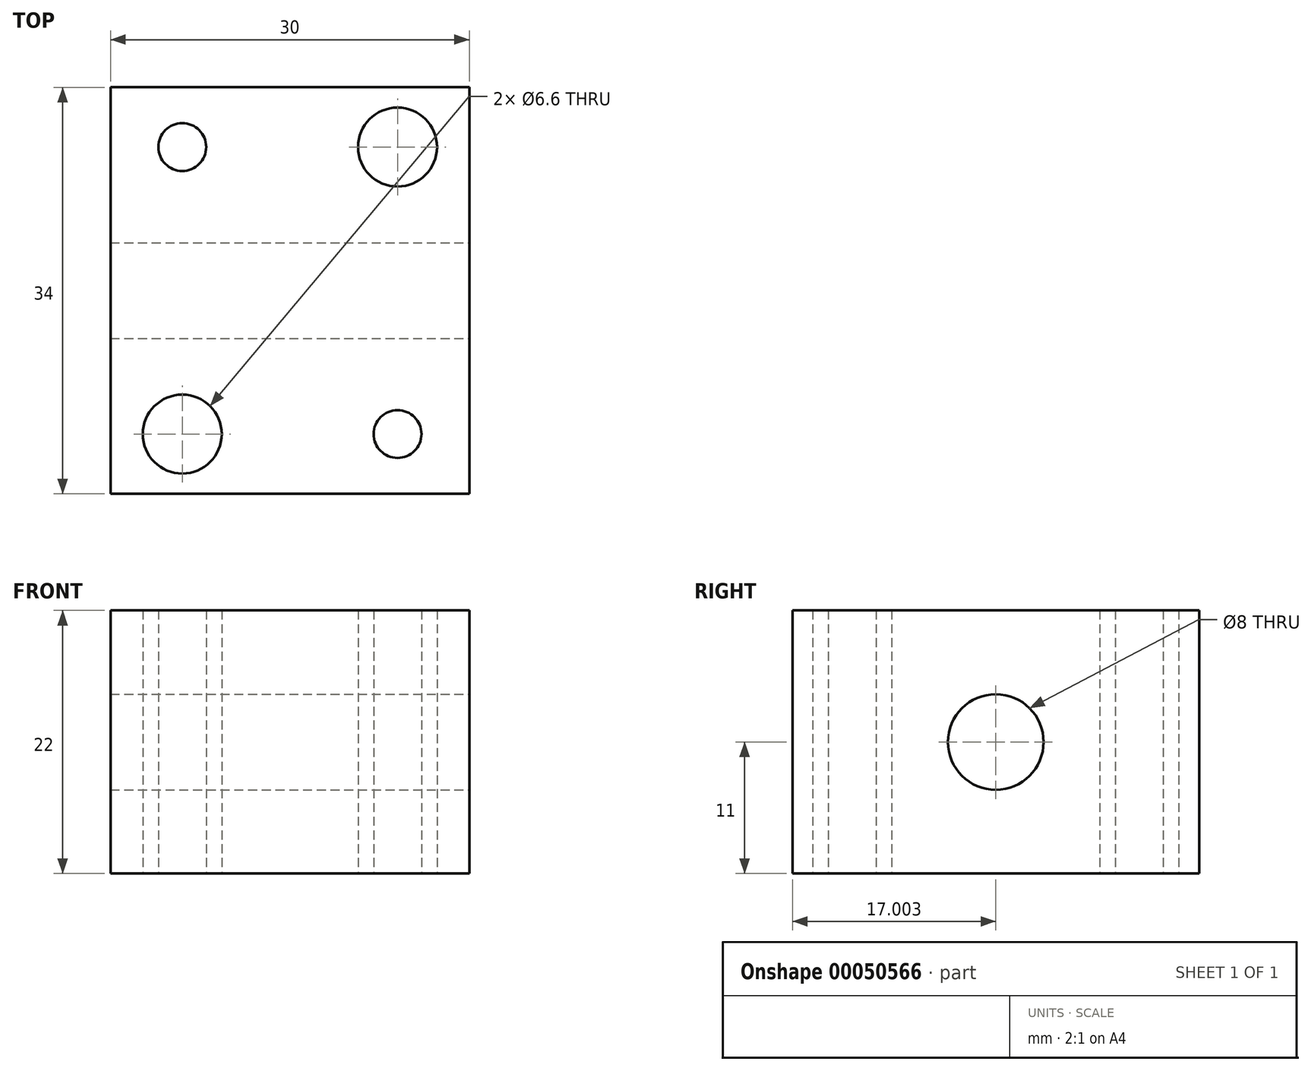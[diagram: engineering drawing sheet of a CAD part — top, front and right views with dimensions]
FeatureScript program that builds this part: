
annotation { "Feature Type Name" : "Feature", "Feature Type Description" : "" }
export const myFeature = defineFeature(function(context is Context, id is Id, definition is map)
    precondition{}
    {
        {
            var Q0;
            Q0=qCreatedBy(makeId("Top.planeOp"),FACE);
            var sketch = newSketch(context, id + "F0", { "sketchPlane" : qUnion([Q0])});
            skLineSegment(sketch, "E0.bottom", {"start": v(-13, 20.28) * mm, "end": v(17, 20.28) * mm});
            skLineSegment(sketch, "E0.top", {"start": v(-13, -13.72) * mm, "end": v(17, -13.72) * mm});
            skLineSegment(sketch, "E0.left", {"start": v(-13, 20.28) * mm, "end": v(-13, -13.72) * mm});
            skLineSegment(sketch, "E0.right", {"start": v(17, 20.28) * mm, "end": v(17, -13.72) * mm});
            skLineSegment(sketch, "E1.0", {"start": v(-7, 20.28) * mm, "end": v(-7, -13.72) * mm, "construction": true});
            skLineSegment(sketch, "E2.0", {"start": v(11, 20.28) * mm, "end": v(11, -13.72) * mm, "construction": true});
            skLineSegment(sketch, "E3.0", {"start": v(-13, 15.28) * mm, "end": v(17, 15.28) * mm, "construction": true});
            skLineSegment(sketch, "E4.0", {"start": v(-13, -8.72) * mm, "end": v(17, -8.72) * mm, "construction": true});
            skCircle(sketch, "E5", {"center": v(-7, 15.28) * mm, "radius": 2 * mm});
            skCircle(sketch, "E6", {"center": v(-7, 15.28) * mm, "radius": 3.3 * mm});
            skLineSegment(sketch, "E7", {"start": v(2, 20.28) * mm, "end": v(2, -13.72) * mm, "construction": true});
            skLineSegment(sketch, "E8", {"start": v(17, 3.28) * mm, "end": v(-13, 3.28) * mm, "construction": true});
            skCircle(sketch, "E9.MirrorC", {"center": v(11, 15.28) * mm, "radius": 3.3 * mm});
            skCircle(sketch, "E10.MirrorC", {"center": v(11, 15.28) * mm, "radius": 2 * mm});
            skCircle(sketch, "E11.MirrorC", {"center": v(11, -8.72) * mm, "radius": 3.3 * mm});
            skCircle(sketch, "E12.MirrorC", {"center": v(11, -8.72) * mm, "radius": 2 * mm});
            skCircle(sketch, "E13.MirrorC", {"center": v(-7, -8.72) * mm, "radius": 3.3 * mm});
            skCircle(sketch, "E14.MirrorC", {"center": v(-7, -8.72) * mm, "radius": 2 * mm});
            skSolve(sketch);
        }
        {
            var Q0;
            Q0=makeQuery(id+"F0.imprint","IMPRINT",FACE,{"disambiguationData":[TD([[makeQuery(id+"F0.imprint","IMPRINT",EDGE,{"derivedFrom":sQuery(id+"F0.wireOp",EDGE,"E0.bottom")}),-1.0]])]});
            var Q1;
            Q1=makeQuery(id+"F0.imprint","IMPRINT",FACE,{"disambiguationData":[TD([[makeQuery(id+"F0.imprint","IMPRINT",EDGE,{"derivedFrom":sQuery(id+"F0.wireOp",EDGE,"E13.MirrorC")}),-1.0]])]});
            var Q2;
            Q2=makeQuery(id+"F0.imprint","IMPRINT",FACE,{"disambiguationData":[TD([[makeQuery(id+"F0.imprint","IMPRINT",EDGE,{"derivedFrom":sQuery(id+"F0.wireOp",EDGE,"E5")}),-1.0]])]});
            var Q3;
            Q3=makeQuery(id+"F0.imprint","IMPRINT",FACE,{"disambiguationData":[TD([[makeQuery(id+"F0.imprint","IMPRINT",EDGE,{"derivedFrom":sQuery(id+"F0.wireOp",EDGE,"E9.MirrorC")}),-1.0]])]});
            var Q4;
            Q4=makeQuery(id+"F0.imprint","IMPRINT",FACE,{"disambiguationData":[TD([[makeQuery(id+"F0.imprint","IMPRINT",EDGE,{"derivedFrom":sQuery(id+"F0.wireOp",EDGE,"E11.MirrorC")}),1.0]])]});
            extrude(context, id + "F1", {"entities" : qUnion([Q0, Q1, Q2, Q3, Q4]), "depth" : 22 * mm});
        }
        {
            var Q0;
            Q0=makeQuery(id+"F1.opExtrude","SWEPT_FACE",FACE,{"disambiguationData":[OSD([sQuery(id+"F0.wireOp",EDGE,"E0.right")])]});
            cPlane(context, id + "F2", {"entities" : qUnion([Q0]), "cplaneType" : CPlaneType.OFFSET, "offset" : 0 * mm, "width" : 150 * mm, "height" : 150 * mm});
        }
        {
            var Q0;
            Q0=qCreatedBy(id+"F2.planeOp",FACE);
            var sketch = newSketch(context, id + "F3", { "sketchPlane" : qUnion([Q0])});
            skLineSegment(sketch, "E15.0.0", {"start": v(-13.72, 0) * mm, "end": v(20.28, 0) * mm});
            skLineSegment(sketch, "E15.0.1", {"start": v(20.28, 0) * mm, "end": v(20.28, 22) * mm});
            skLineSegment(sketch, "E15.0.2", {"start": v(20.28, 22) * mm, "end": v(-13.72, 22) * mm});
            skLineSegment(sketch, "E15.0.3", {"start": v(-13.72, 22) * mm, "end": v(-13.72, 0) * mm});
            skLineSegment(sketch, "E16.0", {"start": v(-13.72, 11) * mm, "end": v(20.28, 11) * mm, "construction": true});
            skPoint(sketch, "E17", {"position": v(3.28, 11) * mm});
            skSolve(sketch);
        }
        {
            var Q0;
            Q0=sQuery(id+"F3.wireOp",VERTEX,"E17");
            var Q1;
            Q1=makeQuery(id+"F1.opExtrude","SWEPT_BODY",BODY,{"disambiguationData":[OSD([sQuery(id+"F0.wireOp",EDGE,"E0.bottom"),sQuery(id+"F0.wireOp",EDGE,"E0.top"),sQuery(id+"F0.wireOp",EDGE,"E0.left"),sQuery(id+"F0.wireOp",EDGE,"E0.right"),sQuery(id+"F0.wireOp",EDGE,"E5"),sQuery(id+"F0.wireOp",EDGE,"E10.MirrorC"),sQuery(id+"F0.wireOp",EDGE,"E12.MirrorC"),sQuery(id+"F0.wireOp",EDGE,"E14.MirrorC")])]});
            hole(context, id + "F4", {"style" : HoleStyle.SIMPLE, "holeDiameter" : 8 * mm, "endStyle" : HoleEndStyle.THROUGH, "locations" : qUnion([Q0]), "scope" : qUnion([Q1])});
        }
    });
